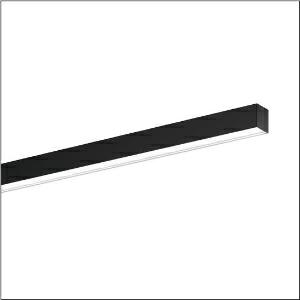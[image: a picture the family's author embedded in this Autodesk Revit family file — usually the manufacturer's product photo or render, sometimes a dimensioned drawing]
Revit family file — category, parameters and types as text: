
# Revit family: silica_r__21_51mx23dc4abb_ae3b
name_source: partatom
category: Lighting Fixtures
units: mm (PartAtom-declared; Revit-internal decimal feet)

## family parameters
Cut with Voids When Loaded = No
Host = Face
Light Source = No
Part Type = Normal
Room Calculation Point = No
Round Connector Dimension = Use Diameter
Shared = No

## types (1)
- --- (1 x LED, 8200 lm, 58.2 W, 4000K)
    Apparent Load = 58 VA
    CIE Flux Codes = 78 96 99 100 100
    Color Rendering = 80
    Color Temperature = 4000K
    Default Elevation = 1800 mm
    Description = Silica® 21, office luminaire, primary optical cover: prismatic diffuser, of PMMA, CAT 2 (L<= 3000cd/m²), light emission: direct distribution, primary light characteristic: symmetric, installation type: surface-mounted, LED, rated luminous flux: 8.200lm, luminous efficacy: 141lm/W, light colour: 840, colour temperature: 4000K, with terminal, 3+2-pole, max. 2.5mm², mains connection: 220..240V, AC, 50/60Hz, rated input power: 58.2W, luminaire housing, of aluminium, jet black (RAL 9005), length: 3.004mm, width: 53mm, height: 53mm, protection rating (complete): IP20, insulation class (complete): insulation class I (protective earthing), certification: CE, permissible operating ambient temperature: 0..+35°C, standard: EN 50419, packaging unit: 1 piece
    Height = 0 mm  [stored 0 ft]
    Lamp = 1 x LED
    Lamp Light Flux = 8200 lm
    Lamp Power = 58.2 W
    Lamp count = 1
    Length = 3004 mm
    Luminous efficacy = 141 lm/W
    Manufacturer = Siteco
    ModVariant = No
    Model = 51MX23DC4ABB
    Mounting Place = Ceiling
    Mounting Type = Recessed
    Number of Poles = 1
    OnlyDefault = Yes
    Power Factor = 1
    Product Name = Silica® 21
    Product group = office luminaire | ceiling recessed
    ProductGroupID = 401
    Protection Class = Protection class I
    Protection Degree = IP 20
    RLX_Detail_Level = 1
    RLX_Emergency_Light_Flux = 0 lm
    RLX_Emergency_Type = 0
    RLX_Emergency_Type_DB = No
    RlxData = <blob elided: 23649 chars, md5=9d615373>
    Socket = socket
    Standby Power = 0 W
    System Light Flux = 8200 lm
    System Power = 58 W
    Type Comments = factory setting: luminous flux: 100 % | dim-lin: 254 | 323 mA
    Type Image = l_1297760.jpg
    URL = http://relux.com
    VarID = @adj_049865
    Voltage = 0 V
    Weight = 0.00 kg
    Width = 53 mm

note: [stored X ft] marks values corroborated as IEEE doubles in the binary element streams (Revit-internal decimal feet)

## geometry (parser evidence)
native form markers: Blend x4, Sweep x9
no freeform markers — native parametric forms only
